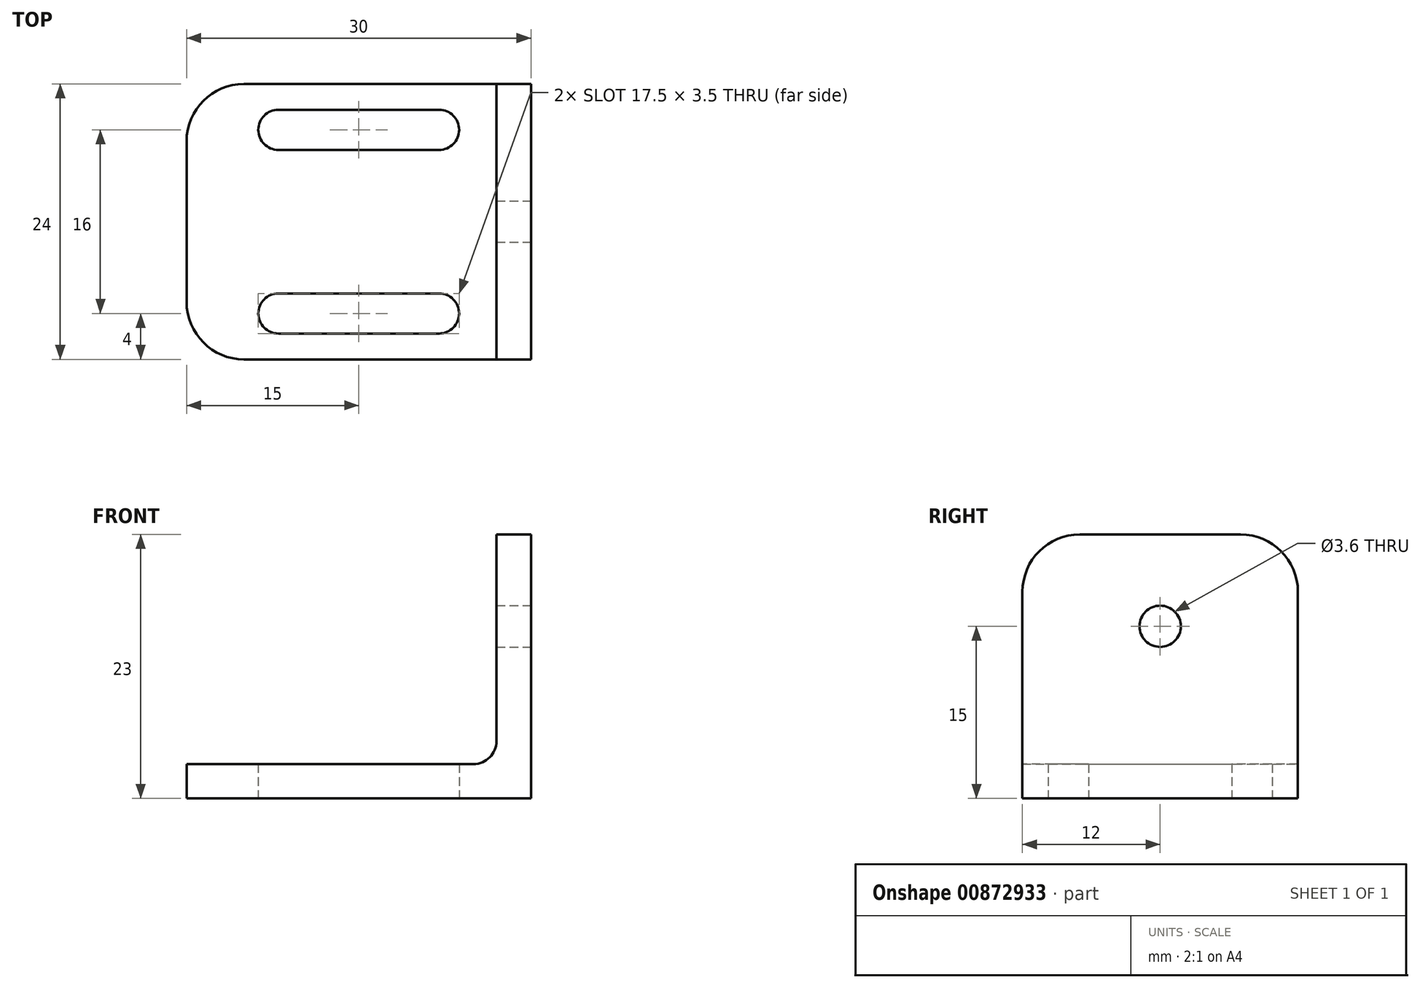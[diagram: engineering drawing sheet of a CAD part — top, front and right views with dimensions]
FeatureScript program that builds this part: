
annotation { "Feature Type Name" : "Feature", "Feature Type Description" : "" }
export const myFeature = defineFeature(function(context is Context, id is Id, definition is map)
    precondition{}
    {
        {
            var Q0;
            Q0=qCreatedBy(makeId("Front.planeOp"),FACE);
            var sketch = newSketch(context, id + "F0", { "sketchPlane" : qUnion([Q0])});
            skLineSegment(sketch, "E0", {"start": v(0, 0) * mm, "end": v(-30, 0) * mm});
            skLineSegment(sketch, "E1", {"start": v(-30, 0) * mm, "end": v(-30, 3) * mm});
            skLineSegment(sketch, "E2", {"start": v(-30, 3) * mm, "end": v(-3, 3) * mm});
            skLineSegment(sketch, "E3", {"start": v(-3, 3) * mm, "end": v(-3, 23) * mm});
            skLineSegment(sketch, "E4", {"start": v(-3, 23) * mm, "end": v(0, 23) * mm});
            skLineSegment(sketch, "E5", {"start": v(0, 23) * mm, "end": v(0, 0) * mm});
            skSolve(sketch);
        }
        {
            var Q0;
            Q0=makeQuery(id+"F0.imprint","IMPRINT",FACE,{"disambiguationData":[TD([[makeQuery(id+"F0.imprint","IMPRINT",EDGE,{"derivedFrom":sQuery(id+"F0.wireOp",EDGE,"E0")}),-1.0]])]});
            extrude(context, id + "F1", {"entities" : qUnion([Q0]), "depth" : 24 * mm, "offsetDistance" : 25 * mm});
        }
        {
            var Q0;
            Q0=makeQuery(id+"F1.opExtrude","SWEPT_EDGE",EDGE,{"disambiguationData":[OSD([sQuery(id+"F0.wireOp",EDGE,"E2"),sQuery(id+"F0.wireOp",EDGE,"E3")])]});
            fillet(context, id + "F2", {"entities" : qUnion([Q0]), "radius" : 2 * mm, "tangentPropagation" : true, "allowEdgeOverflow" : false});
        }
        {
            var Q0;
            Q0=makeQuery(id+"F1.opExtrude","SWEPT_FACE",FACE,{"disambiguationData":[OSD([sQuery(id+"F0.wireOp",EDGE,"E5")])]});
            var sketch = newSketch(context, id + "F3", { "sketchPlane" : qUnion([Q0])});
            skCircle(sketch, "E6", {"center": v(-12, 15) * mm, "radius": 1.8 * mm});
            skLineSegment(sketch, "E7", {"start": v(-12, 23) * mm, "end": v(-12, 0) * mm, "construction": true});
            skSolve(sketch);
        }
        {
            var Q0;
            Q0=makeQuery(id+"F3.imprint","IMPRINT",FACE,{"disambiguationData":[TD([[makeQuery(id+"F3.imprint","IMPRINT",EDGE,{"derivedFrom":sQuery(id+"F3.wireOp",EDGE,"E6")}),1.0]])]});
            extrude(context, id + "F4", {"entities" : qUnion([Q0]), "operationType" : NewBodyOperationType.REMOVE, "endBound" : BoundingType.THROUGH_ALL, "oppositeDirection" : true, "depth" : 25 * mm, "offsetDistance" : 25 * mm});
        }
        {
            var Q0;
            Q0=makeQuery(id+"F1.opExtrude","CAP_EDGE",EDGE,{"disambiguationData":[OSD([sQuery(id+"F0.wireOp",EDGE,"E4")])],"isStart":false});
            var Q1;
            Q1=makeQuery(id+"F1.opExtrude","CAP_EDGE",EDGE,{"disambiguationData":[OSD([sQuery(id+"F0.wireOp",EDGE,"E4")])],"isStart":true});
            var Q2;
            Q2=makeQuery(id+"F1.opExtrude","CAP_EDGE",EDGE,{"disambiguationData":[OSD([sQuery(id+"F0.wireOp",EDGE,"E1")])],"isStart":false});
            var Q3;
            Q3=makeQuery(id+"F1.opExtrude","CAP_EDGE",EDGE,{"disambiguationData":[OSD([sQuery(id+"F0.wireOp",EDGE,"E1")])],"isStart":true});
            fillet(context, id + "F5", {"entities" : qUnion([Q0, Q1, Q2, Q3]), "radius" : 5 * mm, "tangentPropagation" : true, "allowEdgeOverflow" : false});
        }
        {
            var Q0;
            Q0=makeQuery(id+"F1.opExtrude","SWEPT_FACE",FACE,{"disambiguationData":[OSD([sQuery(id+"F0.wireOp",EDGE,"E0")])]});
            var sketch = newSketch(context, id + "F6", { "sketchPlane" : qUnion([Q0])});
            skLineSegment(sketch, "E8", {"start": v(-8, 20) * mm, "end": v(-22, 20) * mm, "construction": true});
            skLineSegment(sketch, "E9", {"start": v(0, 12) * mm, "end": v(-30, 12) * mm, "construction": true});
            skArc(sketch, "E10.0.startCap", {"start": v(-8, 21.75) * mm, "mid": v(-6.25, 20) * mm, "end": v(-8, 18.25) * mm});
            skArc(sketch, "E10.0.endCap", {"start": v(-22, 18.25) * mm, "mid": v(-23.75, 20) * mm, "end": v(-22, 21.75) * mm});
            skLineSegment(sketch, "E10.0.left", {"start": v(-8, 18.25) * mm, "end": v(-22, 18.25) * mm});
            skLineSegment(sketch, "E10.0.right", {"start": v(-8, 21.75) * mm, "end": v(-22, 21.75) * mm});
            skLineSegment(sketch, "E11.MirrorCS", {"start": v(-8, 2.25) * mm, "end": v(-22, 2.25) * mm});
            skLineSegment(sketch, "E12.MirrorCS", {"start": v(-8, 5.75) * mm, "end": v(-22, 5.75) * mm});
            skArc(sketch, "E13.MirrorCS", {"start": v(-22, 5.75) * mm, "mid": v(-23.75, 4) * mm, "end": v(-22, 2.25) * mm});
            skArc(sketch, "E14.MirrorCS", {"start": v(-8, 2.25) * mm, "mid": v(-6.25, 4) * mm, "end": v(-8, 5.75) * mm});
            skLineSegment(sketch, "E15.MirrorCS", {"start": v(-8, 4) * mm, "end": v(-22, 4) * mm, "construction": true});
            skSolve(sketch);
        }
        {
            var Q0;
            Q0 = qSketchRegion(id + "F6", true);
            extrude(context, id + "F7", {"entities" : qUnion([Q0]), "operationType" : NewBodyOperationType.REMOVE, "endBound" : BoundingType.THROUGH_ALL, "oppositeDirection" : true, "depth" : 25 * mm, "offsetDistance" : 25 * mm});
        }
    });
